# Revit family: Haworth_Fern_Stool
name_source: partatom
category: Furniture
revit_build: Autodesk Revit 2018 (Build: 20170223_1515(x64)
units: mm (PartAtom-declared; Revit-internal decimal feet)

## family parameters
Always vertical = Yes
Cut with Voids When Loaded = No
OmniClass Number = 23.40.20.00
OmniClass Title = General Furniture and Specialties
Room Calculation Point = No
Shared = No
Work Plane-Based = No

## types (4) — shared parameters
Assembly Code = E2020200
Caster Finish = Haworth _ Polymer _ Fog
Depth = 2' - 0"
Description = Haworth Fern Stool - 4D Arms
Hardware Finish = Haworth _ Polymer _ Black
Height = 3' - 8"
Manufacturer = Haworth
Model = SFS-U0
Post Finish = Haworth _ Metal _ Polished Aluminum
URL = http://www.haworth.com
URL - Product = https://www.haworth.com
Version = 2
Warranty = http://www.haworth.com
Width = 2' - 4"

## per-type parameters (varying)
| type | 4D Arms | Adjustable Arms | Arms | Fixed Arms | Height Adjustable Arms | Without Arms |
| SFS-U0-7 - 4D Arms | Yes | Yes | Yes | No | No | No |
| SFS-U0-1 - Fixed Arms | No | No | Yes | Yes | No | No |
| SFS-U0-4 - Height Adjustable Arms | No | Yes | Yes | No | Yes | No |
| SFS-U0-0 - Without Arms | No | No | No | No | No | Yes |

## geometry (parser evidence)
native form markers: Sweep x11
no freeform markers — native parametric forms only
